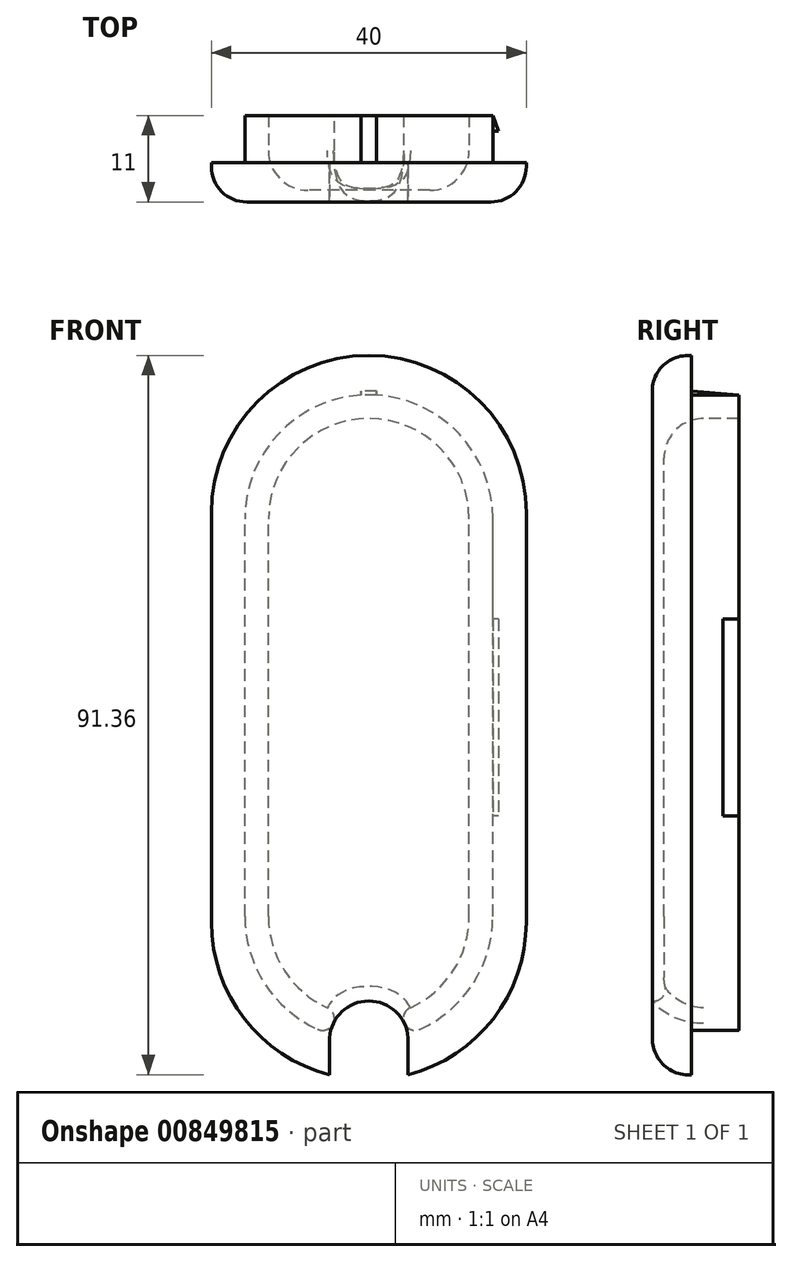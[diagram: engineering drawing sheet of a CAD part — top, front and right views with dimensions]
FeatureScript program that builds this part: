
annotation { "Feature Type Name" : "Feature", "Feature Type Description" : "" }
export const myFeature = defineFeature(function(context is Context, id is Id, definition is map)
    precondition{}
    {
        {
            var Q0;
            Q0=qCreatedBy(makeId("Front.planeOp"),FACE);
            var sketch = newSketch(context, id + "F0", { "sketchPlane" : qUnion([Q0])});
            skLineSegment(sketch, "E0.bottom", {"start": v(20, -46) * mm, "end": v(-20, -46) * mm});
            skLineSegment(sketch, "E0.top", {"start": v(20, 46) * mm, "end": v(-20, 46) * mm});
            skLineSegment(sketch, "E0.left", {"start": v(20, -46) * mm, "end": v(20, 46) * mm});
            skLineSegment(sketch, "E0.right", {"start": v(-20, -46) * mm, "end": v(-20, 46) * mm});
            skPoint(sketch, "E0.middle", {"position": v(0, 0) * mm});
            skSolve(sketch);
        }
        {
            var Q0;
            Q0=qSketchRegion(id+"F0",true);
            extrude(context, id + "F1", {"entities" : qUnion([Q0]), "depth" : 5 * mm, "offsetDistance" : 25 * mm});
        }
        {
            var Q0;
            Q0=makeQuery(id+"F1.opExtrude","SWEPT_EDGE",EDGE,{"disambiguationData":[OSD([sQuery(id+"F0.wireOp",EDGE,"E0.top"),sQuery(id+"F0.wireOp",EDGE,"E0.right")])]});
            var Q1;
            Q1=makeQuery(id+"F1.opExtrude","SWEPT_EDGE",EDGE,{"disambiguationData":[OSD([sQuery(id+"F0.wireOp",EDGE,"E0.top"),sQuery(id+"F0.wireOp",EDGE,"E0.left")])]});
            var Q2;
            Q2=makeQuery(id+"F1.opExtrude","SWEPT_EDGE",EDGE,{"disambiguationData":[OSD([sQuery(id+"F0.wireOp",EDGE,"E0.bottom"),sQuery(id+"F0.wireOp",EDGE,"E0.left")])]});
            var Q3;
            Q3=makeQuery(id+"F1.opExtrude","SWEPT_EDGE",EDGE,{"disambiguationData":[OSD([sQuery(id+"F0.wireOp",EDGE,"E0.bottom"),sQuery(id+"F0.wireOp",EDGE,"E0.right")])]});
            fillet(context, id + "F2", {"entities" : qUnion([Q0, Q1, Q2, Q3]), "radius" : 20 * mm, "tangentPropagation" : true, "allowEdgeOverflow" : false});
        }
        {
            var Q0;
            Q0=makeQuery(id+"F1.opExtrude","CAP_EDGE",EDGE,{"disambiguationData":[OSD([sQuery(id+"F0.wireOp",EDGE,"E0.left")])],"isStart":false});
            fillet(context, id + "F3", {"entities" : qUnion([Q0]), "radius" : 4.5 * mm, "tangentPropagation" : true, "allowEdgeOverflow" : false});
        }
        {
            var Q0;
            Q0=makeQuery(id+"F1.opExtrude","CAP_FACE",FACE,{"disambiguationData":[OSD([sQuery(id+"F0.wireOp",EDGE,"E0.bottom"),sQuery(id+"F0.wireOp",EDGE,"E0.top"),sQuery(id+"F0.wireOp",EDGE,"E0.left"),sQuery(id+"F0.wireOp",EDGE,"E0.right")])],"isStart":true});
            var sketch = newSketch(context, id + "F4", { "sketchPlane" : qUnion([Q0])});
            skLineSegment(sketch, "E1.bottom", {"start": v(0, -41) * mm, "end": v(0, -41) * mm});
            skLineSegment(sketch, "E1.top", {"start": v(0, 41) * mm, "end": v(0, 41) * mm});
            skLineSegment(sketch, "E1.left", {"start": v(15.75, -25.25) * mm, "end": v(15.75, 25.25) * mm});
            skLineSegment(sketch, "E1.right", {"start": v(-15.75, -25.25) * mm, "end": v(-15.75, 25.25) * mm});
            skPoint(sketch, "E1.middle", {"position": v(0, 0) * mm});
            skPoint(sketch, "E2.visualSharp", {"position": v(-15.75, 41) * mm});
            skArc(sketch, "E2.filletArc", {"start": v(0, 41) * mm, "mid": v(-11.14, 36.39) * mm, "end": v(-15.75, 25.25) * mm});
            skPoint(sketch, "E3.visualSharp", {"position": v(15.75, 41) * mm});
            skArc(sketch, "E3.filletArc", {"start": v(15.75, 25.25) * mm, "mid": v(11.14, 36.39) * mm, "end": v(0, 41) * mm});
            skPoint(sketch, "E4.visualSharp", {"position": v(-15.75, -41) * mm});
            skArc(sketch, "E4.filletArc", {"start": v(-15.75, -25.25) * mm, "mid": v(-11.14, -36.39) * mm, "end": v(0, -41) * mm});
            skPoint(sketch, "E5.visualSharp", {"position": v(15.75, -41) * mm});
            skArc(sketch, "E5.filletArc", {"start": v(0, -41) * mm, "mid": v(11.14, -36.39) * mm, "end": v(15.75, -25.25) * mm});
            skArc(sketch, "E6.0", {"start": v(0, -38) * mm, "mid": v(9.02, -34.27) * mm, "end": v(12.75, -25.25) * mm});
            skArc(sketch, "E6.1", {"start": v(12.75, 25.25) * mm, "mid": v(9.02, 34.27) * mm, "end": v(0, 38) * mm});
            skArc(sketch, "E6.2", {"start": v(0, 38) * mm, "mid": v(-9.02, 34.27) * mm, "end": v(-12.75, 25.25) * mm});
            skLineSegment(sketch, "E6.3", {"start": v(12.75, -25.25) * mm, "end": v(12.75, 25.25) * mm});
            skLineSegment(sketch, "E6.4", {"start": v(-12.75, -25.25) * mm, "end": v(-12.75, 25.25) * mm});
            skArc(sketch, "E6.5", {"start": v(-12.75, -25.25) * mm, "mid": v(-9.02, -34.27) * mm, "end": v(0, -38) * mm});
            skSolve(sketch);
        }
        {
            var Q0;
            Q0=qSketchRegion(id+"F4",true);
            extrude(context, id + "F5", {"entities" : qUnion([Q0]), "operationType" : NewBodyOperationType.ADD, "depth" : 6 * mm, "offsetDistance" : 25 * mm});
        }
        {
            var Q0;
            Q0=qCreatedBy(makeId("Top.planeOp"),FACE);
            var sketch = newSketch(context, id + "F6", { "sketchPlane" : qUnion([Q0])});
            skLineSegment(sketch, "E7.0.1", {"start": v(-15.75, 6) * mm, "end": v(15.75, 6) * mm});
            skLineSegment(sketch, "E7.0.3", {"start": v(-15.75, 6) * mm, "end": v(15.75, 6) * mm});
            skLineSegment(sketch, "E8", {"start": v(15.75, 6) * mm, "end": v(15.75, 4) * mm});
            skLineSegment(sketch, "E9", {"start": v(15.75, 4) * mm, "end": v(16.5, 4) * mm});
            skLineSegment(sketch, "E10", {"start": v(16.5, 4) * mm, "end": v(15.75, 6) * mm});
            skSolve(sketch);
        }
        {
            var Q0;
            Q0=qSketchRegion(id+"F6",true);
            extrude(context, id + "F7", {"entities" : qUnion([Q0]), "operationType" : NewBodyOperationType.ADD, "endBound" : BoundingType.SYMMETRIC, "depth" : 25 * mm, "offsetDistance" : 25 * mm});
        }
        {
            var Q0;
            Q0=qCreatedBy(makeId("Right.planeOp"),FACE);
            var sketch = newSketch(context, id + "F8", { "sketchPlane" : qUnion([Q0])});
            skLineSegment(sketch, "E11.0.0", {"start": v(6, -12.5) * mm, "end": v(6, -25.25) * mm});
            skLineSegment(sketch, "E11.0.1", {"start": v(6, -25.25) * mm, "end": v(6, -41) * mm});
            skLineSegment(sketch, "E11.0.2", {"start": v(6, -25.25) * mm, "end": v(6, -12.5) * mm});
            skLineSegment(sketch, "E11.0.3", {"start": v(6, -12.5) * mm, "end": v(6, 12.5) * mm});
            skLineSegment(sketch, "E11.0.4", {"start": v(6, 12.5) * mm, "end": v(6, 25.25) * mm});
            skLineSegment(sketch, "E11.0.5", {"start": v(6, 25.25) * mm, "end": v(6, 41) * mm});
            skLineSegment(sketch, "E11.0.6", {"start": v(6, 25.25) * mm, "end": v(6, 12.5) * mm});
            skLineSegment(sketch, "E11.0.7", {"start": v(6, 12.5) * mm, "end": v(6, -12.5) * mm});
            skLineSegment(sketch, "E12", {"start": v(0, 41) * mm, "end": v(0, 41.5) * mm});
            skLineSegment(sketch, "E13", {"start": v(0, 41.5) * mm, "end": v(6, 41) * mm});
            skLineSegment(sketch, "E14", {"start": v(6, 41) * mm, "end": v(6, 40) * mm});
            skLineSegment(sketch, "E15", {"start": v(6, 40) * mm, "end": v(0, 40) * mm});
            skLineSegment(sketch, "E16", {"start": v(0, 40) * mm, "end": v(0, 41) * mm});
            skSolve(sketch);
        }
        {
            var Q0;
            Q0=makeQuery(id+"F8.imprint","IMPRINT",FACE,{"disambiguationData":[TD([[makeQuery(id+"F8.imprint","IMPRINT",EDGE,{"derivedFrom":sQuery(id+"F8.wireOp",EDGE,"E12")}),-1.0]])]});
            extrude(context, id + "F9", {"entities" : qUnion([Q0]), "operationType" : NewBodyOperationType.ADD, "endBound" : BoundingType.SYMMETRIC, "depth" : 2 * mm, "offsetDistance" : 25 * mm});
        }
        {
            var Q0;
            Q0=makeQuery(id+"F5.boolean.opBoolean","SPLIT",FACE,{"disambiguationData":[TD([makeQuery(id+"F5.opExtrude","SWEPT_FACE",FACE,{"disambiguationData":[OSD([sQuery(id+"F4.wireOp",EDGE,"E6.3")])]})])],"derivedFrom":makeQuery(id+"F1.opExtrude","CAP_FACE",FACE,{"disambiguationData":[OSD([sQuery(id+"F0.wireOp",EDGE,"E0.bottom"),sQuery(id+"F0.wireOp",EDGE,"E0.top"),sQuery(id+"F0.wireOp",EDGE,"E0.left"),sQuery(id+"F0.wireOp",EDGE,"E0.right")])],"isStart":true})});
            extrude(context, id + "F10", {"entities" : qUnion([Q0]), "operationType" : NewBodyOperationType.REMOVE, "oppositeDirection" : true, "depth" : 3.5 * mm, "offsetDistance" : 25 * mm});
        }
        {
            var Q0;
            Q0=makeQuery(id+"F10.boolean.opBoolean","COPY",FACE,{"derivedFrom":makeQuery(id+"F10.opExtrude","CAP_FACE",FACE,{"disambiguationData":[OSD([sQuery(id+"F0.wireOp",EDGE,"E0.bottom"),sQuery(id+"F0.wireOp",EDGE,"E0.top"),sQuery(id+"F0.wireOp",EDGE,"E0.left"),sQuery(id+"F0.wireOp",EDGE,"E0.right")])],"isStart":false})});
            fillet(context, id + "F11", {"entities" : qUnion([Q0]), "radius" : 5 * mm, "tangentPropagation" : true, "allowEdgeOverflow" : false});
        }
        {
            var Q0;
            {var subQ0=sQuery(id+"F8.wireOp",EDGE,"E14");Q0=makeQuery(id+"FkPRSlewJA9MnwW_1.1.F9.boolean.opBoolean","MERGE",FACE,{"derivedFrom":[makeQuery(id+"F9.boolean.opBoolean","MERGE",FACE,{"derivedFrom":[makeQuery(id+"F5.opExtrude","CAP_FACE",FACE,{"disambiguationData":[OSD([sQuery(id+"F4.wireOp",EDGE,"E1.left"),sQuery(id+"F4.wireOp",EDGE,"E1.right"),sQuery(id+"F4.wireOp",EDGE,"E2.filletArc"),sQuery(id+"F4.wireOp",EDGE,"E3.filletArc"),sQuery(id+"F4.wireOp",EDGE,"E4.filletArc"),sQuery(id+"F4.wireOp",EDGE,"E5.filletArc"),sQuery(id+"F4.wireOp",EDGE,"E6.0"),sQuery(id+"F4.wireOp",EDGE,"E6.1"),sQuery(id+"F4.wireOp",EDGE,"E6.2"),sQuery(id+"F4.wireOp",EDGE,"E6.3"),sQuery(id+"F4.wireOp",EDGE,"E6.4"),sQuery(id+"F4.wireOp",EDGE,"E6.5")])],"isStart":false}),makeQuery(id+"F9.opExtrude","SWEPT_FACE",FACE,{"disambiguationData":[OSD([subQ0])]})]}),makeQuery(id+"FkPRSlewJA9MnwW_1.1.F9.opExtrude","SWEPT_FACE",FACE,{"disambiguationData":[OSD([subQ0])]})]});}
            var sketch = newSketch(context, id + "F12", { "sketchPlane" : qUnion([Q0])});
            skArc(sketch, "E17", {"start": v(5, -41) * mm, "mid": v(0, -36) * mm, "end": v(-5, -41) * mm});
            skLineSegment(sketch, "E18", {"start": v(0, -41) * mm, "end": v(-19.15, -41) * mm, "construction": true});
            skLineSegment(sketch, "E19", {"start": v(0, -41) * mm, "end": v(12.2, -41) * mm, "construction": true});
            skLineSegment(sketch, "E20", {"start": v(-5, -41) * mm, "end": v(-5, -49.74) * mm});
            skLineSegment(sketch, "E21", {"start": v(5, -41) * mm, "end": v(5, -49.74) * mm});
            skLineSegment(sketch, "E22", {"start": v(5, -49.74) * mm, "end": v(-5, -49.74) * mm});
            skSolve(sketch);
        }
        {
            var Q0;
            Q0 = qSketchRegion(id + "F12", true);
            extrude(context, id + "F13", {"entities" : qUnion([Q0]), "operationType" : NewBodyOperationType.REMOVE, "endBound" : BoundingType.THROUGH_ALL, "oppositeDirection" : true, "depth" : 25 * mm, "offsetDistance" : 25 * mm});
        }
        {
            var Q0;
            {var subQ1=sQuery(id+"F4.wireOp",EDGE,"E1.right");var subQ2=sQuery(id+"F4.wireOp",EDGE,"E5.filletArc");var subQ3=sQuery(id+"F4.wireOp",EDGE,"E4.filletArc");Q0=makeQuery(id+"F13.boolean.opBoolean","INTERSECT",EDGE,{"derivedFrom":[makeQuery(id+"FkPRSlewJA9MnwW_1.1.F9.boolean.opBoolean","SPLIT",FACE,{"disambiguationData":[TD([makeQuery(id+"F5.opExtrude","SWEPT_FACE",FACE,{"disambiguationData":[OSD([subQ1])]})])],"derivedFrom":makeQuery(id+"F5.opExtrude","SWEPT_FACE",FACE,{"disambiguationData":[OSD([subQ3,subQ2])]})}),makeQuery(id+"F13.opExtrude","SWEPT_FACE",FACE,{"disambiguationData":[OSD([sQuery(id+"F12.wireOp",EDGE,"E17")])]})]});}
            var Q1;
            {var subQ0=sQuery(id+"F4.wireOp",EDGE,"E6.5");var subQ1=sQuery(id+"F4.wireOp",EDGE,"E6.0");Q1=makeQuery(id+"F13.boolean.opBoolean","INTERSECT",EDGE,{"disambiguationData":[OD(1.0)],"derivedFrom":[makeQuery(id+"F10.boolean.opBoolean","MERGE",FACE,{"derivedFrom":[makeQuery(id+"F5.opExtrude","SWEPT_FACE",FACE,{"disambiguationData":[OSD([subQ1,subQ0])]}),makeQuery(id+"F10.opExtrude","SWEPT_FACE",FACE,{"disambiguationData":[OSD([subQ1,subQ0])]})]}),makeQuery(id+"F13.opExtrude","SWEPT_FACE",FACE,{"disambiguationData":[OSD([sQuery(id+"F12.wireOp",EDGE,"E17")])]})]});}
            var Q2;
            {var subQ1=sQuery(id+"F4.wireOp",EDGE,"E1.left");var subQ2=sQuery(id+"F4.wireOp",EDGE,"E5.filletArc");var subQ3=sQuery(id+"F4.wireOp",EDGE,"E4.filletArc");Q2=makeQuery(id+"F13.boolean.opBoolean","INTERSECT",EDGE,{"derivedFrom":[makeQuery(id+"FkPRSlewJA9MnwW_1.1.F9.boolean.opBoolean","SPLIT",FACE,{"disambiguationData":[TD([makeQuery(id+"F5.opExtrude","SWEPT_FACE",FACE,{"disambiguationData":[OSD([subQ1])]})])],"derivedFrom":makeQuery(id+"F5.opExtrude","SWEPT_FACE",FACE,{"disambiguationData":[OSD([subQ3,subQ2])]})}),makeQuery(id+"F13.opExtrude","SWEPT_FACE",FACE,{"disambiguationData":[OSD([sQuery(id+"F12.wireOp",EDGE,"E17")])]})]});}
            fillet(context, id + "F14", {"entities" : qUnion([Q0, Q1, Q2]), "radius" : 1.5 * mm, "tangentPropagation" : true, "allowEdgeOverflow" : false});
        }
    });
